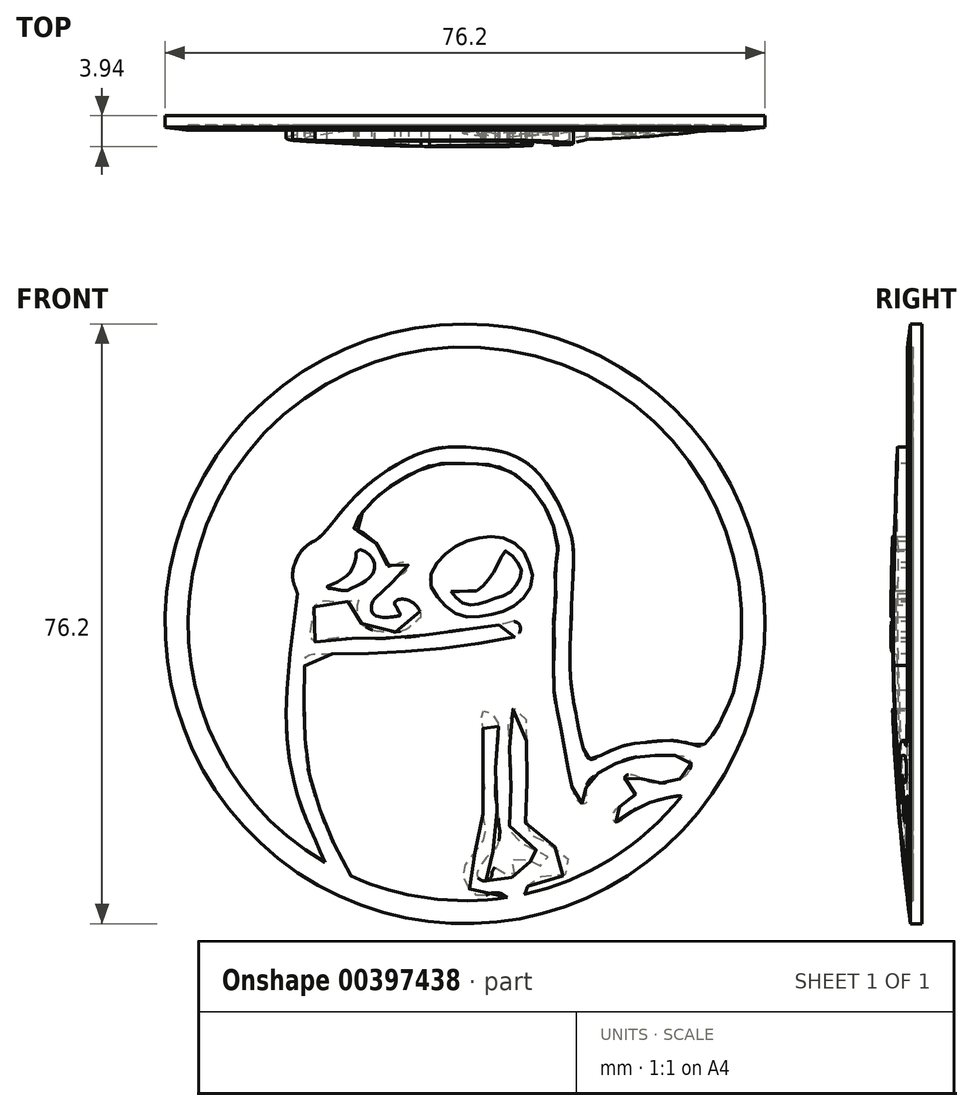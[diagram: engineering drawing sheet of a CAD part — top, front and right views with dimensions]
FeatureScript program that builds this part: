
annotation { "Feature Type Name" : "Feature", "Feature Type Description" : "" }
export const myFeature = defineFeature(function(context is Context, id is Id, definition is map)
    precondition{}
    {
        {
            var Q0;
            Q0=qCreatedBy(makeId("Front.planeOp"),FACE);
            var sketch = newSketch(context, id + "F0", { "sketchPlane" : qUnion([Q0])});
            skCircle(sketch, "E0", {"center": v(0, 0) * mm, "radius": 41.28 * mm});
            skArc(sketch, "E1", {"start": v(-15.7, -34.72) * mm, "mid": v(-5.14, -37.75) * mm, "end": v(5.84, -37.65) * mm});
            skFitSpline(sketch, "E2", {"points": [v(-19.29, -32.86) * mm, v(-20.97, -28.94) * mm, v(-22.72, -24.57) * mm, v(-24.26, -17.86) * mm, v(-24.5, -9.16) * mm, v(-23.07, 4.17) * mm], "startDerivative": vector(-10.89, 25.44) * mm, "endDerivative": vector(6.46, 50.7) * mm});
            skFitSpline(sketch, "E3", {"points": [v(-23.07, 4.17) * mm, v(-23.7, 6.25) * mm, v(-23.4, 8.35) * mm, v(-22.43, 10.12) * mm, v(-20.66, 11.43) * mm], "startDerivative": vector(-3.05, 9.11) * mm, "endDerivative": vector(8.76, 3.77) * mm});
            skFitSpline(sketch, "E4", {"points": [v(-20.66, 11.43) * mm, v(-20.14, 11.8) * mm, v(-18.59, 13.44) * mm, v(-16.68, 15.84) * mm, v(-13.22, 19.25) * mm, v(-9.29, 21.98) * mm, v(-4.83, 23.93) * mm, v(-0.8, 24.33) * mm, v(3.79, 23.95) * mm, v(7.1, 22.96) * mm], "startDerivative": vector(9.62, 5.7) * mm, "endDerivative": vector(22.89, -12.21) * mm});
            skFitSpline(sketch, "E5", {"points": [v(7.1, 22.96) * mm, v(8.35, 22.25) * mm, v(9.8, 21.03) * mm, v(11.63, 18.66) * mm, v(13.13, 16.07) * mm, v(14.34, 13.03) * mm, v(14.87, 10.67) * mm, v(14.8, 5.29) * mm, v(14.52, -1.36) * mm, v(14.42, -5.76) * mm], "startDerivative": vector(17.16, -8.92) * mm, "endDerivative": vector(0.8, -34.81) * mm});
            skFitSpline(sketch, "E6", {"points": [v(14.42, -5.76) * mm, v(14.56, -8.05) * mm, v(15.2, -12.12) * mm, v(15.93, -15.67) * mm, v(16.36, -17.36) * mm, v(16.72, -18.19) * mm, v(17.14, -18.62) * mm, v(17.84, -18.53) * mm, v(19.47, -17.72) * mm, v(21.82, -16.79) * mm, v(24.29, -16.37) * mm, v(27.88, -16.06) * mm, v(29.83, -16.23) * mm, v(31.42, -16.6) * mm, v(31.85, -16.75) * mm, v(32.52, -16.79) * mm, v(33.21, -16.3) * mm, v(34.86, -14) * mm, v(36.92, -9.42) * mm], "startDerivative": vector(1.24, -34.63) * mm, "endDerivative": vector(21.35, 54.06) * mm});
            skFitSpline(sketch, "E7", {"points": [v(-15.7, -34.72) * mm, v(-16.36, -33.38) * mm, v(-17.1, -32) * mm, v(-18.4, -29.6) * mm, v(-19.13, -27.9) * mm, v(-20.19, -24.87) * mm, v(-21.09, -21.97) * mm, v(-21.9, -18.06) * mm, v(-22.09, -13.52) * mm, v(-22.15, -11.53) * mm, v(-22.1, -5.39) * mm, v(-22.08, -4.88) * mm, v(-21.93, -4.57) * mm, v(-21.69, -4.36) * mm, v(-21.34, -4.2) * mm, v(-20.64, -4.16) * mm, v(-14.4, -4.12) * mm, v(-11.54, -4) * mm, v(-5.4, -3.62) * mm, v(0.5, -2.88) * mm, v(6.25, -1.94) * mm, v(6.93, -1.72) * mm, v(7.31, -1.45) * mm, v(7.57, -1.05) * mm, v(7.6, -0.42) * mm, v(7.38, 0) * mm, v(6.75, 0.31) * mm, v(5.37, 0) * mm, v(3.27, -0.36) * mm, v(0.46, -0.72) * mm, v(-1.92, -1.04) * mm, v(-5.34, -1.52) * mm, v(-8.43, -1.87) * mm, v(-11.07, -1.98) * mm, v(-15, -2.01) * mm, v(-17.83, -1.97) * mm, v(-19.06, -2.19) * mm, v(-20.2, -2.45) * mm, v(-20.82, -2.43) * mm, v(-21.28, -1.93) * mm, v(-21.22, -0.82) * mm, v(-20.92, 1.33) * mm, v(-20.7, 2.41) * mm, v(-20.22, 2.94) * mm, v(-19.75, 3.2) * mm, v(-18.44, 3.09) * mm, v(-16.66, 3.02) * mm, v(-15.56, 3.17) * mm, v(-14.96, 3.37) * mm, v(-14.73, 3.37) * mm, v(-14.63, 3.27) * mm, v(-14.78, 3) * mm, v(-14.86, 1.9) * mm, v(-14.8, 1.2) * mm, v(-14.54, 0.45) * mm, v(-14.23, 0) * mm, v(-13.59, -0.46) * mm, v(-12.74, -0.83) * mm, v(-11.42, -1.03) * mm, v(-9.96, -1.1) * mm, v(-8.92, -1.02) * mm, v(-8.03, -0.68) * mm, v(-7.17, 0) * mm, v(-6.18, 0.84) * mm, v(-6.08, 0.9) * mm, v(-6.08, 1.42) * mm, v(-6.46, 2.14) * mm, v(-6.98, 2.78) * mm, v(-7.85, 3.25) * mm, v(-8.5, 3.4) * mm, v(-9.24, 3.28) * mm, v(-9.67, 2.92) * mm, v(-9.5, 2.43) * mm, v(-9.09, 1.67) * mm, v(-8.95, 1.41) * mm, v(-8.88, 1.2) * mm, v(-9.47, 1.02) * mm, v(-10.77, 0.9) * mm, v(-11.73, 0.95) * mm, v(-12.43, 1.22) * mm, v(-12.8, 1.68) * mm, v(-12.82, 2.76) * mm, v(-12.48, 3.4) * mm], "startDerivative": vector(-53.04, 103.01) * mm, "endDerivative": vector(38.6, 61.83) * mm});
            skFitSpline(sketch, "E8", {"points": [v(-12.48, 3.4) * mm, v(-12.06, 3.86) * mm, v(-11.08, 4.77) * mm, v(-9.89, 5.8) * mm, v(-8.58, 6.92) * mm, v(-8.08, 7.33) * mm, v(-8.02, 7.47) * mm, v(-8, 7.63) * mm, v(-7.86, 7.87) * mm, v(-7.8, 8.06) * mm, v(-8.07, 8.33) * mm, v(-8.41, 8.44) * mm, v(-9.25, 8.25) * mm, v(-10.3, 7.74) * mm, v(-10.48, 7.75) * mm, v(-10.68, 8.13) * mm, v(-11.1, 9.18) * mm, v(-11.67, 10.27) * mm, v(-12.33, 11.2) * mm, v(-13.12, 11.97) * mm, v(-14.03, 12.53) * mm, v(-14.8, 12.77) * mm, v(-15.05, 12.93) * mm, v(-15.28, 13.14) * mm, v(-15.32, 13.67) * mm, v(-15.02, 14.23) * mm, v(-13.84, 15.7) * mm, v(-12.48, 17.15) * mm, v(-11, 18.4) * mm, v(-9.4, 19.5) * mm, v(-7.35, 20.67) * mm, v(-5.48, 21.5) * mm, v(-4.3, 21.9) * mm, v(-2.27, 22.08) * mm, v(1.65, 21.99) * mm, v(3.9, 21.82) * mm, v(5.34, 21.37) * mm, v(6.57, 20.78) * mm, v(8.49, 19.35) * mm, v(9.92, 17.72) * mm, v(11.18, 15.77) * mm, v(11.8, 14.58) * mm, v(12.27, 13.16) * mm, v(12.7, 11.13) * mm, v(12.8, 10.07) * mm, v(12.63, 8.85) * mm, v(12.43, 7.65) * mm, v(12.48, 5.69) * mm, v(12.4, 2) * mm, v(12.1, 0) * mm, v(12.27, -1.57) * mm, v(12.16, -6.55) * mm, v(12.23, -9.22) * mm], "startDerivative": vector(27.13, 32) * mm, "endDerivative": vector(6.26, -75.07) * mm});
            skFitSpline(sketch, "E9", {"points": [v(12.22, -9.1) * mm, v(12.35, -10.16) * mm, v(12.72, -12.13) * mm, v(13.25, -14.7) * mm, v(13.84, -18.02) * mm, v(14.38, -20.86) * mm, v(14.78, -22.73) * mm, v(15.16, -23.84) * mm, v(15.59, -24.43) * mm, v(15.96, -24.66) * mm, v(16.36, -24.76) * mm, v(16.67, -24.63) * mm, v(16.87, -24.37) * mm, v(16.78, -23.78) * mm, v(16.65, -22.83) * mm, v(16.83, -21.92) * mm, v(17.93, -20.8) * mm, v(19.4, -19.91) * mm, v(21.18, -19.01) * mm, v(23.33, -18.38) * mm, v(25.27, -18.16) * mm, v(29.85, -18.2) * mm, v(30.64, -18.51) * mm, v(31.03, -18.9) * mm, v(31.1, -19.46) * mm, v(30.8, -20.32) * mm, v(30.29, -20.95) * mm, v(29.43, -21.41) * mm, v(28.14, -21.78) * mm, v(27.13, -21.9) * mm, v(25.86, -21.88) * mm, v(24.8, -21.58) * mm, v(23.86, -21.1) * mm, v(23.15, -20.84) * mm, v(22.35, -20.8) * mm, v(22.07, -21) * mm, v(21.99, -21.2) * mm, v(22.03, -21.5) * mm, v(22.4, -21.96) * mm, v(22.83, -22.36) * mm, v(23.24, -22.77) * mm, v(23.42, -23.01) * mm, v(23.44, -23.55) * mm, v(22.75, -24.13) * mm, v(21.87, -24.7) * mm, v(20.83, -25.52) * mm, v(20.36, -26) * mm, v(20.29, -26.53) * mm, v(20.44, -27.12) * mm, v(20.78, -27.29) * mm, v(21.26, -27.2) * mm, v(21.84, -26.82) * mm, v(22.5, -26.2) * mm, v(23.46, -25.47) * mm, v(24.7, -24.82) * mm, v(26.27, -24.34) * mm, v(28.08, -23.9) * mm, v(29.46, -23.7) * mm, v(29.82, -23.72) * mm], "startDerivative": vector(6.25, -55.49) * mm, "endDerivative": vector(27.91, -1.77) * mm});
            skFitSpline(sketch, "E10", {"points": [v(28.08, -23.9) * mm, v(29.34, -23.63) * mm, v(29.86, -23.66) * mm], "startDerivative": vector(2.27, 0.58) * mm, "endDerivative": vector(1.15, -0.12) * mm});
            skFitSpline(sketch, "E11", {"points": [v(5.84, -37.65) * mm, v(5.32, -37.33) * mm, v(4.82, -37.07) * mm, v(3.98, -37.02) * mm, v(3.59, -37.09) * mm, v(2.84, -37.36) * mm, v(2.12, -37.45) * mm, v(1.47, -37.3) * mm, v(0.8, -36.75) * mm, v(0.14, -35.7) * mm, v(-0.22, -34.9) * mm, v(-0.2, -33.8) * mm, v(0.46, -32.65) * mm, v(1.74, -31) * mm, v(2.53, -29.83) * mm, v(2.81, -29.1) * mm, v(2.8, -27.79) * mm, v(2.47, -26.09) * mm, v(2.39, -24.42) * mm, v(2.64, -22.95) * mm, v(2.74, -22.53) * mm, v(2.63, -21.67) * mm, v(2.5, -21.11) * mm, v(2.5, -20.41) * mm, v(2.57, -19.28) * mm, v(2.6, -17.71) * mm, v(2.44, -16.5) * mm, v(2.46, -14.93) * mm, v(2.5, -14.2) * mm, v(2.38, -13.25) * mm, v(2.19, -12.77) * mm, v(2.36, -12.26) * mm, v(2.62, -11.95) * mm, v(3.12, -11.93) * mm, v(3.8, -12.4) * mm, v(4.42, -13.28) * mm, v(4.6, -14.26) * mm, v(4.6, -15.9) * mm, v(4.48, -16.8) * mm, v(4.43, -18.2) * mm, v(4.3, -18.66) * mm, v(4.2, -22.9) * mm, v(4.27, -24.2) * mm, v(4.37, -24.7) * mm, v(4.4, -25.64) * mm, v(4.54, -26.25) * mm, v(4.6, -27.07) * mm, v(4.67, -27.76) * mm, v(4.78, -28.32) * mm, v(4.73, -29.36) * mm, v(4.6, -30) * mm, v(4.3, -30.69) * mm, v(3.84, -31.34) * mm, v(3.6, -31.59) * mm, v(3.24, -31.9) * mm, v(2.78, -32.37) * mm, v(2.3, -33.05) * mm, v(1.95, -33.57) * mm, v(1.73, -34.07) * mm, v(1.63, -34.49) * mm, v(1.73, -34.88) * mm, v(2.05, -35.18) * mm, v(2.38, -35.34) * mm, v(2.97, -35.34) * mm, v(3.35, -35.12) * mm, v(3.67, -34.7) * mm, v(3.7, -34.23) * mm, v(3.9, -33.8) * mm, v(4.23, -33.44) * mm, v(4.63, -33.18) * mm, v(5.08, -33.55) * mm, v(5.4, -34.1) * mm, v(5.5, -34.4) * mm, v(5.78, -34.64) * mm, v(6.27, -34.85) * mm, v(6.6, -34.86) * mm, v(6.75, -34.49) * mm, v(6.86, -34.2) * mm, v(6.93, -33.9) * mm, v(6.73, -33.42) * mm, v(6.48, -32.74) * mm, v(6.48, -32.5) * mm, v(6.85, -32.16) * mm, v(7.3, -31.99) * mm, v(7.9, -32.09) * mm, v(8.63, -32.48) * mm, v(9.17, -32.77) * mm, v(9.5, -33) * mm, v(9.85, -33.18) * mm, v(10.3, -33.28) * mm, v(10.78, -33.24) * mm, v(11.2, -32.96) * mm, v(11.46, -32.74) * mm, v(11.51, -32.37) * mm, v(11.33, -31.99) * mm, v(10.14, -31.27) * mm, v(8.2, -30.42) * mm, v(6.99, -29.82) * mm, v(6.4, -29.23) * mm, v(6.22, -28.7) * mm, v(6.15, -27.89) * mm, v(6.28, -22.96) * mm, v(6.5, -21.03) * mm, v(6.6, -20.36) * mm, v(6.45, -19.87) * mm, v(6.2, -19.24) * mm, v(6.08, -18.93) * mm, v(6.09, -17.59) * mm, v(6.14, -17.14) * mm, v(6.15, -15.19) * mm, v(6.06, -14.2) * mm, v(5.88, -12.95) * mm, v(6, -12.27) * mm, v(6.47, -11.8) * mm, v(6.9, -11.66) * mm, v(7.35, -11.7) * mm, v(7.93, -12.2) * mm, v(8.33, -12.86) * mm, v(8.4, -13.89) * mm, v(8.47, -17.74) * mm, v(8.52, -20.4) * mm, v(8.56, -22.42) * mm, v(8.48, -25.37) * mm, v(8.39, -25.79) * mm, v(8.39, -26.92) * mm, v(8.3, -27.5) * mm, v(8.45, -28.15) * mm, v(8.87, -28.86) * mm, v(9.45, -29.4) * mm, v(10.4, -29.73) * mm, v(11.27, -30.14) * mm, v(12.5, -30.8) * mm, v(13.52, -31.7) * mm, v(14.4, -32.6) * mm, v(14.72, -33.21) * mm, v(14.37, -34.15) * mm, v(13.72, -34.6) * mm, v(12.69, -34.8) * mm, v(11.19, -34.84) * mm, v(9.8, -34.88) * mm, v(9.24, -35.08) * mm, v(8.87, -35.39) * mm, v(8.59, -36.14) * mm, v(8.13, -37.22) * mm], "startDerivative": vector(-91.64, 48.63) * mm, "endDerivative": vector(-71.66, -81.6) * mm});
            skFitSpline(sketch, "E12", {"points": [v(8.04, -37.24) * mm, v(8.29, -36.86) * mm, v(8.59, -36.14) * mm], "startDerivative": vector(0.63, 0.7) * mm, "endDerivative": vector(0.5, 1.38) * mm});
            skFitSpline(sketch, "E13", {"points": [v(-18.86, 5.24) * mm, v(-17.96, 5.57) * mm, v(-17.12, 6.01) * mm, v(-16.23, 6.62) * mm, v(-15.54, 7.52) * mm, v(-15.16, 8.52) * mm, v(-14.97, 9.3) * mm, v(-14.95, 9.86) * mm, v(-14.6, 10.16) * mm, v(-14.36, 10.22) * mm, v(-13.72, 9.92) * mm, v(-13.26, 9.6) * mm, v(-12.76, 9.05) * mm, v(-12.51, 8.5) * mm, v(-12.41, 7.85) * mm, v(-12.57, 7.11) * mm, v(-13.08, 6.39) * mm, v(-13.95, 5.73) * mm, v(-15.09, 5.15) * mm, v(-15.84, 4.78) * mm, v(-16.17, 4.62) * mm, v(-17.2, 4.63) * mm, v(-18.22, 4.83) * mm, v(-18.92, 4.98) * mm, v(-18.86, 5.24) * mm]});
            skFitSpline(sketch, "E14", {"points": [v(-4.66, 5.14) * mm, v(-4.85, 5.6) * mm, v(-4.78, 6.54) * mm, v(-4.2, 7.87) * mm, v(-3.17, 9.13) * mm, v(-1.7, 10.36) * mm, v(-0.36, 11.12) * mm, v(0.83, 11.57) * mm, v(2.77, 11.93) * mm, v(4.62, 11.98) * mm, v(6.15, 11.47) * mm, v(7.41, 10.64) * mm, v(8.22, 9.77) * mm, v(8.57, 9.13) * mm, v(8.95, 8) * mm, v(9.2, 7.53) * mm, v(9.23, 5.77) * mm, v(8.76, 4.63) * mm, v(7.93, 3.42) * mm, v(6.45, 2.28) * mm, v(5.13, 1.64) * mm, v(3.35, 1.22) * mm, v(0, 0.97) * mm, v(-1.3, 1.47) * mm, v(-2.3, 2.16) * mm, v(-3.6, 3.42) * mm, v(-4.66, 5.14) * mm]});
            skFitSpline(sketch, "E15", {"points": [v(-1.92, 4.42) * mm, v(0.39, 4.52) * mm, v(1.37, 4.55) * mm, v(1.83, 4.6) * mm, v(2.33, 5.03) * mm, v(3.36, 6.24) * mm, v(4.14, 7.43) * mm, v(4.76, 8.68) * mm, v(5.16, 9.68) * mm, v(5.39, 9.95) * mm, v(5.56, 10.04) * mm, v(5.78, 9.99) * mm, v(6.3, 9.55) * mm, v(6.87, 8.97) * mm, v(7.38, 8.23) * mm, v(7.69, 7.55) * mm, v(7.77, 6.87) * mm, v(7.38, 5.89) * mm, v(6.48, 4.6) * mm, v(5.51, 3.94) * mm, v(4.61, 3.66) * mm, v(3.85, 3.42) * mm, v(2.78, 3.03) * mm, v(1.75, 2.72) * mm, v(0.84, 2.61) * mm, v(0.08, 2.68) * mm, v(-0.58, 3) * mm, v(-1.77, 4.13) * mm, v(-1.92, 4.3) * mm, v(-1.98, 4.39) * mm, v(-1.92, 4.42) * mm]});
            skArc(sketch, "E16.trimOffspring", {"start": v(8.04, -37.24) * mm, "mid": v(20.13, -32.35) * mm, "end": v(29.86, -23.66) * mm});
            skArc(sketch, "E17.trimOffspring", {"start": v(36.92, -9.42) * mm, "mid": v(-14.66, 35.16) * mm, "end": v(-19.29, -32.86) * mm});
            skLineSegment(sketch, "E18", {"start": v(-20.67, 11.43) * mm, "end": v(-20.66, 11.43) * mm});
            skLineSegment(sketch, "E19", {"start": v(7.1, 22.96) * mm, "end": v(7.1, 22.96) * mm});
            skSolve(sketch);
        }
        {
            var Q0;
            Q0=qCreatedBy(makeId("Front.planeOp"),FACE);
            var sketch = newSketch(context, id + "F1", { "sketchPlane" : qUnion([Q0])});
            skCircle(sketch, "E20", {"center": v(0, 0) * mm, "radius": 41.28 * mm});
            skSolve(sketch);
        }
        {
            var Q0;
            Q0=qSketchRegion(id+"F1",true);
            extrude(context, id + "F2", {"entities" : qUnion([Q0]), "depth" : 5.08 * mm, "hasSecondDirection" : true, "secondDirectionOppositeDirection" : true, "secondDirectionDepth" : 1.27 * mm});
        }
        {
            var Q0;
            Q0=makeQuery(id+"F0.imprint","IMPRINT",FACE,{"disambiguationData":[TD([[makeQuery(id+"F0.imprint","IMPRINT",EDGE,{"derivedFrom":sQuery(id+"F0.wireOp",EDGE,"E1")}),1.0]])]});
            var Q1;
            Q1=makeQuery(id+"F0.imprint","IMPRINT",FACE,{"disambiguationData":[TD([[makeQuery(id+"F0.imprint","IMPRINT",EDGE,{"derivedFrom":sQuery(id+"F0.wireOp",EDGE,"E15")}),-1.0]])]});
            var Q2;
            Q2=makeQuery(id+"F0.imprint","IMPRINT",FACE,{"disambiguationData":[TD([[makeQuery(id+"F0.imprint","IMPRINT",EDGE,{"derivedFrom":sQuery(id+"F0.wireOp",EDGE,"E13")}),-1.0]])]});
            extrude(context, id + "F3", {"entities" : qUnion([Q0, Q1, Q2]), "operationType" : NewBodyOperationType.REMOVE, "depth" : 12.2 * mm});
        }
        {
            var Q0;
            Q0=makeQuery(id+"F0.imprint","IMPRINT",FACE,{"disambiguationData":[TD([[makeQuery(id+"F0.imprint","IMPRINT",EDGE,{"derivedFrom":sQuery(id+"F0.wireOp",EDGE,"E2")}),1.0]])]});
            extrude(context, id + "F4", {"entities" : qUnion([Q0]), "operationType" : NewBodyOperationType.REMOVE, "depth" : 25.32 * mm});
        }
        {
            var Q0;
            Q0=qCreatedBy(makeId("Top.planeOp"),FACE);
            var sketch = newSketch(context, id + "F5", { "sketchPlane" : qUnion([Q0])});
            skArc(sketch, "E21", {"start": v(-43.54, 0) * mm, "mid": v(-21.82, -2.25) * mm, "end": v(0, -3) * mm});
            skLineSegment(sketch, "E22", {"start": v(-64.55, 0) * mm, "end": v(-62.8, -31.58) * mm});
            skLineSegment(sketch, "E23", {"start": v(-62.8, -31.58) * mm, "end": v(0, -29.86) * mm});
            skLineSegment(sketch, "E24.trimOffspring", {"start": v(-43.54, 0) * mm, "end": v(-64.55, 0) * mm});
            skLineSegment(sketch, "E25", {"start": v(0, -3) * mm, "end": v(0, -18.69) * mm});
            skPoint(sketch, "E25.endSnap0", {"position": v(0, -3) * mm});
            skLineSegment(sketch, "E26", {"start": v(0, -18.69) * mm, "end": v(0, -29.86) * mm});
            skSolve(sketch);
        }
        {
            var Q0;
            Q0=makeQuery(id+"F5.imprint","IMPRINT",FACE,{"disambiguationData":[TD([[makeQuery(id+"F5.imprint","IMPRINT",EDGE,{"derivedFrom":sQuery(id+"F5.wireOp",EDGE,"E21")}),-1.0]])]});
            var Q1;
            Q1=sQuery(id+"F5.wireOp",EDGE,"E25");
            revolve(context, id + "F6", {"operationType" : NewBodyOperationType.REMOVE, "entities" : qUnion([Q0]), "axis" : qUnion([Q1]), "revolveType" : RevolveType.FULL, "oppositeDirection" : true});
        }
        {
            var Q0;
            Q0=makeQuery(id+"F2.opExtrude","SWEPT_BODY",BODY,{"disambiguationData":[OSD([sQuery(id+"F1.wireOp",EDGE,"E20")])]});
            var Q1;
            Q1=qCreatedBy(makeId("Origin.pointOp"),VERTEX);
            transform(context, id + "F7", {"entities" : qUnion([Q0]), "transformType" : TransformType.SCALE_UNIFORMLY, "scale" : .9230769, "scalePoint" : qUnion([Q1]), "makeCopy" : false});
        }
    });
